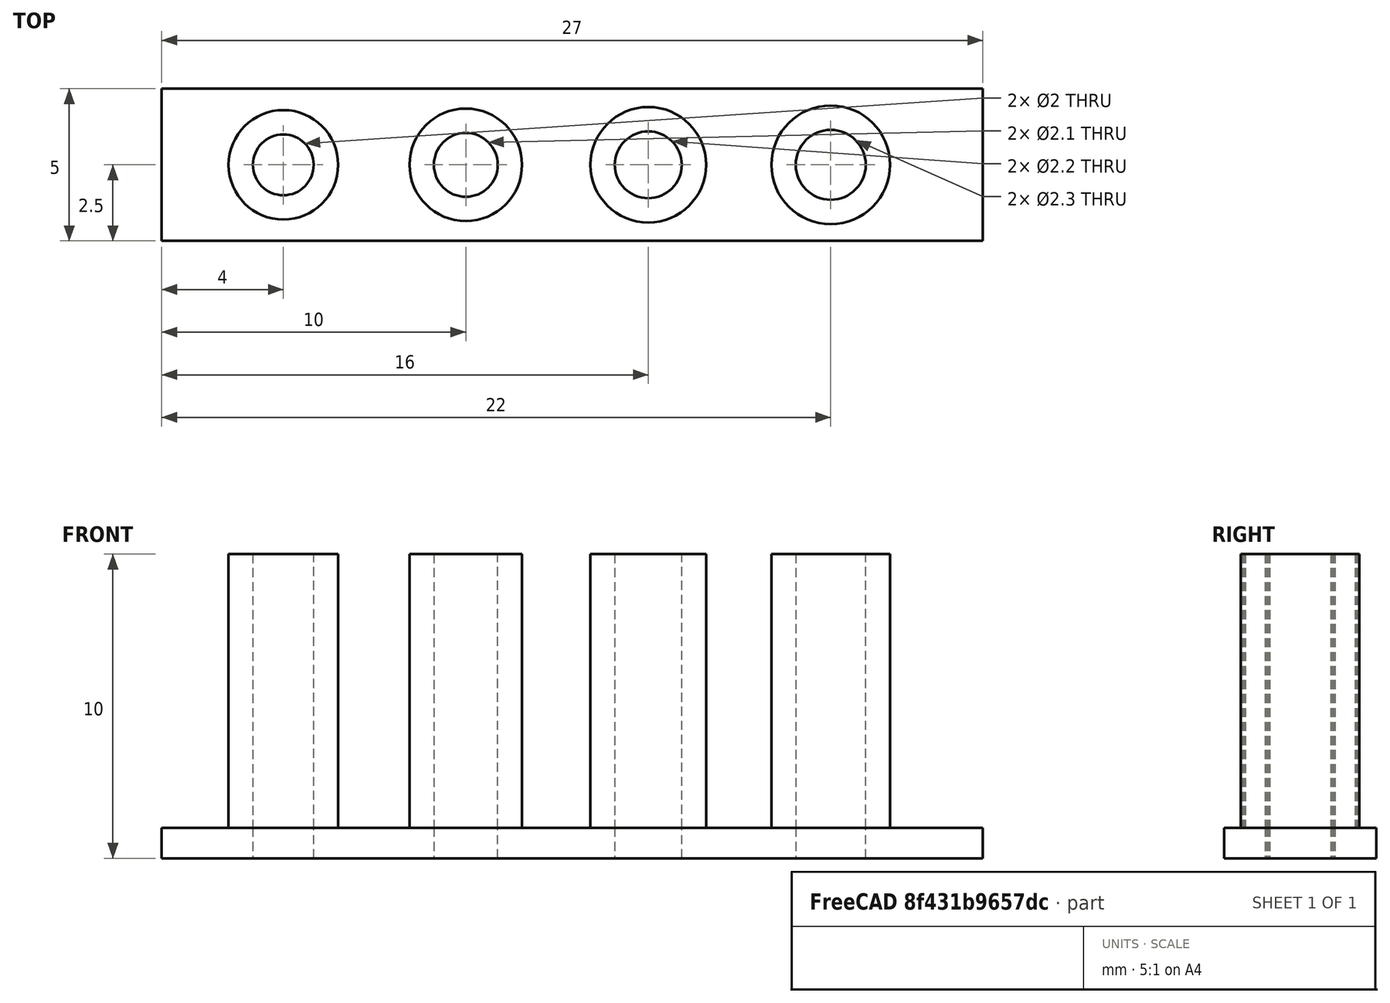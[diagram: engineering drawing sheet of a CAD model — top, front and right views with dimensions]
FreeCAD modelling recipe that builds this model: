
FCSTD DOCUMENT  (FreeCAD 0.20R)
Label: screw_demo
License: All rights reserved
LicenseURL: http://en.wikipedia.org/wiki/All_rights_reserved
objects: Part::Part2DObjectPython×8, PartDesign::Pad×8, Part::Cut×8, Part::Box×5, PartDesign::Thickness×4, PartDesign::Body×4, App::Part×1
note: 49 computed .brp shape members not serialized (recipe doc carries the construction recipe); baked Part::Feature solids carry a one-line shape summary decoded from their .brp

FEATURE [Part::Part2DObjectPython] Circle  # Draft 2D object (typed FeaturePython)
  Area = 3.14159
  FirstAngle = 0
  LastAngle = 0
  MakeFace = true
  Placement = pos=(-10,0,0) rot=(0,0,1;0rad)
  Radius = 1
FEATURE [Part::Part2DObjectPython] Circle001  # Draft 2D object (typed FeaturePython)
  Area = 3.46361
  FirstAngle = 0
  LastAngle = 0
  MakeFace = true
  Placement = pos=(-4,0,0) rot=(0,0,1;0rad)
  Radius = 1.05
FEATURE [Part::Part2DObjectPython] Circle002  # Draft 2D object (typed FeaturePython)
  Area = 3.80133
  FirstAngle = 0
  LastAngle = 0
  MakeFace = true
  Placement = pos=(2,0,0) rot=(0,0,1;0rad)
  Radius = 1.1
FEATURE [Part::Part2DObjectPython] Circle003  # Draft 2D object (typed FeaturePython)
  Area = 4.15476
  FirstAngle = 0
  LastAngle = 0
  MakeFace = true
  Placement = pos=(8,0,0) rot=(0,0,1;0rad)
  Radius = 1.15
FEATURE [PartDesign::Pad] Pad
  Direction = (0,0,1)
  Length = 10
  Length2 = 10
  Placement = pos=(-10,0,0) rot=(0,0,1;0rad)
  Profile = -> Circle
  ReferenceAxis = -> Circle [N_Axis]
  Type = 0
FEATURE [PartDesign::Thickness] Thickness
  Base = -> Pad [Face3]
  BaseFeature = -> Pad
  Intersection = false
  Join = 1
  Mode = 0
  SupportTransform = false
  Value = 0.8
FEATURE [PartDesign::Body] Body
  Group = -> [Circle,Pad,Thickness]
  Origin = -> Origin
  Tip = -> Thickness
FEATURE [PartDesign::Pad] Pad001
  Direction = (0,0,1)
  Length = 10
  Length2 = 10
  Placement = pos=(-4,0,0) rot=(0,0,1;0rad)
  Profile = -> Circle001
  ReferenceAxis = -> Circle001 [N_Axis]
  Type = 0
FEATURE [PartDesign::Thickness] Thickness001
  Base = -> Pad001 [Face3]
  BaseFeature = -> Pad001
  Intersection = false
  Join = 0
  Mode = 0
  SupportTransform = false
  Value = 0.8
FEATURE [PartDesign::Body] Body001
  Group = -> [Circle001,Pad001,Thickness001]
  Origin = -> Origin001
  Tip = -> Thickness001
FEATURE [PartDesign::Pad] Pad002
  Direction = (0,0,1)
  Length = 10
  Length2 = 10
  Placement = pos=(2,0,0) rot=(0,0,1;0rad)
  Profile = -> Circle002
  ReferenceAxis = -> Circle002 [N_Axis]
  Type = 0
FEATURE [PartDesign::Thickness] Thickness002
  Base = -> Pad002 [Face3]
  BaseFeature = -> Pad002
  Intersection = false
  Join = 0
  Mode = 0
  SupportTransform = false
  Value = 0.8
FEATURE [PartDesign::Body] Body002
  Group = -> [Circle002,Pad002,Thickness002]
  Origin = -> Origin002
  Tip = -> Thickness002
FEATURE [PartDesign::Pad] Pad003
  Direction = (0,0,1)
  Length = 10
  Length2 = 10
  Placement = pos=(8,0,0) rot=(0,0,1;0rad)
  Profile = -> Circle003
  ReferenceAxis = -> Circle003 [N_Axis]
  Type = 0
FEATURE [PartDesign::Thickness] Thickness003
  Base = -> Pad003 [Face3]
  BaseFeature = -> Pad003
  Intersection = false
  Join = 0
  Mode = 0
  SupportTransform = false
  Value = 0.8
FEATURE [PartDesign::Body] Body004
  Group = -> [Circle003,Pad003,Thickness003]
  Origin = -> Origin004
  Tip = -> Thickness003
FEATURE [Part::Box] Box  label="Cube"
  AttacherType = Attacher::AttachEngine3D
  Height = 2
  Length = 30
  Placement = pos=(-15,-3,-1) rot=(0,0,1;0rad)
  Width = 5
FEATURE [Part::Cut] Cut
  Base = -> Body
  Tool = -> Box
FEATURE [Part::Box] Box001  label="Cube001"
  AttacherType = Attacher::AttachEngine3D
  Height = 2
  Length = 30
  Placement = pos=(-15,-3,-1) rot=(0,0,1;0rad)
  Width = 5
FEATURE [Part::Cut] Cut001
  Base = -> Body001
  Tool = -> Box001
FEATURE [Part::Box] Box002  label="Cube002"
  AttacherType = Attacher::AttachEngine3D
  Height = 2
  Length = 30
  Placement = pos=(-15,-3,-1) rot=(0,0,1;0rad)
  Width = 5
FEATURE [Part::Cut] Cut002
  Base = -> Body002
  Tool = -> Box002
FEATURE [Part::Box] Box003  label="Cube003"
  AttacherType = Attacher::AttachEngine3D
  Height = 2
  Length = 30
  Placement = pos=(-15,-3,-1) rot=(0,0,1;0rad)
  Width = 5
FEATURE [Part::Cut] Cut003
  Base = -> Body004
  Tool = -> Box003
FEATURE [Part::Box] Box004  label="Cube004"
  AttacherType = Attacher::AttachEngine3D
  Height = 1
  Length = 27
  Placement = pos=(-14,-2.5,0) rot=(0,0,1;0rad)
  Width = 5
FEATURE [Part::Part2DObjectPython] Circle004  # Draft 2D object (typed FeaturePython)
  Area = 3.14159
  FirstAngle = 0
  LastAngle = 0
  MakeFace = true
  Placement = pos=(-10,0,0) rot=(0,0,1;0rad)
  Radius = 1
FEATURE [PartDesign::Pad] Pad004
  Direction = (0,0,1)
  Length = 10
  Length2 = 10
  Placement = pos=(-10,0,0) rot=(0,0,1;0rad)
  Profile = -> Circle004
  ReferenceAxis = -> Circle004 [N_Axis]
  Type = 0
FEATURE [Part::Cut] Cut004
  Base = -> Box004
  Tool = -> Pad004
FEATURE [Part::Part2DObjectPython] Circle005  # Draft 2D object (typed FeaturePython)
  Area = 3.46361
  FirstAngle = 0
  LastAngle = 0
  MakeFace = true
  Placement = pos=(-4,0,0) rot=(0,0,1;0rad)
  Radius = 1.05
FEATURE [PartDesign::Pad] Pad005
  Direction = (0,0,1)
  Length = 10
  Length2 = 10
  Placement = pos=(-4,0,0) rot=(0,0,1;0rad)
  Profile = -> Circle005
  ReferenceAxis = -> Circle005 [N_Axis]
  Type = 0
FEATURE [Part::Cut] Cut005
  Base = -> Cut004
  Tool = -> Pad005
FEATURE [Part::Part2DObjectPython] Circle006  # Draft 2D object (typed FeaturePython)
  Area = 4.15476
  FirstAngle = 0
  LastAngle = 0
  MakeFace = true
  Placement = pos=(8,0,0) rot=(0,0,1;0rad)
  Radius = 1.15
FEATURE [PartDesign::Pad] Pad006
  Direction = (0,0,1)
  Length = 10
  Length2 = 10
  Placement = pos=(8,0,0) rot=(0,0,1;0rad)
  Profile = -> Circle006
  ReferenceAxis = -> Circle006 [N_Axis]
  Type = 0
FEATURE [Part::Cut] Cut006
  Base = -> Cut005
  Tool = -> Pad006
FEATURE [Part::Part2DObjectPython] Circle007  # Draft 2D object (typed FeaturePython)
  Area = 3.80133
  FirstAngle = 0
  LastAngle = 0
  MakeFace = true
  Placement = pos=(2,0,0) rot=(0,0,1;0rad)
  Radius = 1.1
FEATURE [PartDesign::Pad] Pad007
  Direction = (0,0,1)
  Length = 10
  Length2 = 10
  Placement = pos=(2,0,0) rot=(0,0,1;0rad)
  Profile = -> Circle007
  ReferenceAxis = -> Circle007 [N_Axis]
  Type = 0
FEATURE [Part::Cut] Cut007
  Base = -> Cut006
  Tool = -> Pad007
FEATURE [App::Part] Part
  Group = -> [Circle006,Circle005,Pad005,Cut004,Pad004,Circle004,Cut005,Cut006,Circle007,Box004,Pad006,Pad007,Cut007,Box003,Body004,Cut003,Box002,Body002,Cut002,Box001,Body001,Cut001,Body,Box,Cut]
  Origin = -> Origin005
